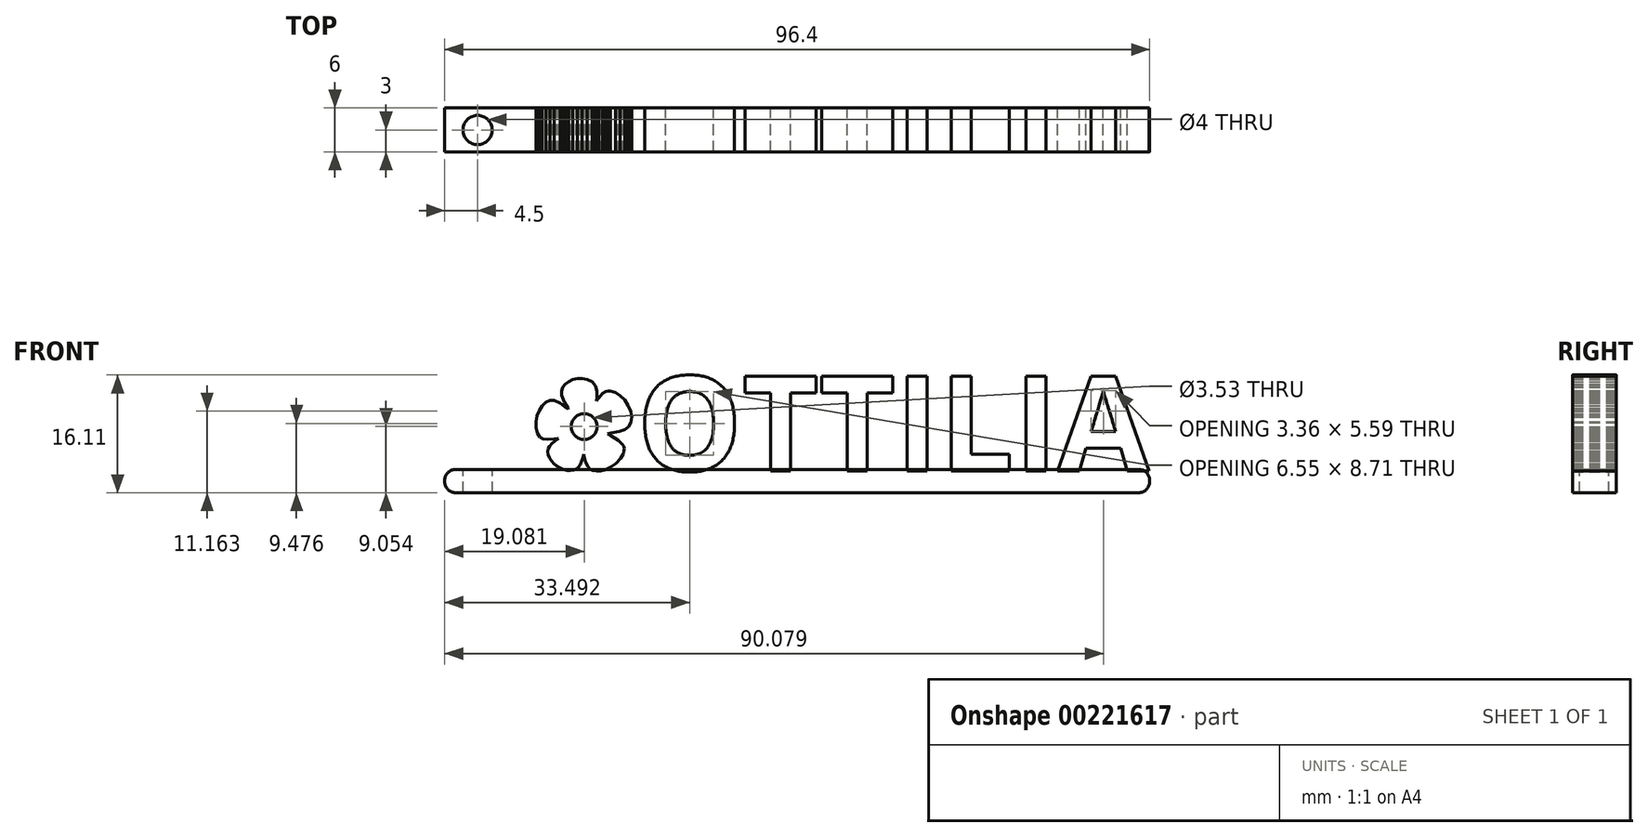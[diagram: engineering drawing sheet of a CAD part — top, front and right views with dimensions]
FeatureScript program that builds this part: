
annotation { "Feature Type Name" : "Feature", "Feature Type Description" : "" }
export const myFeature = defineFeature(function(context is Context, id is Id, definition is map)
    precondition{}
    {
        {
            var Q0;
            Q0=qCreatedBy(makeId("Front.planeOp"),FACE);
            var sketch = newSketch(context, id + "F0", { "sketchPlane" : qUnion([Q0])});
            skText(sketch, "E0", { "text": "    OTTILIA", "fontName": "OpenSans-Bold.ttf"});
            skLineSegment(sketch, "E1.0.0", {"start": v(-9.3, 0.1) * mm, "end": v(-8.53, 0.46) * mm});
            skLineSegment(sketch, "E1.0.1", {"start": v(-8.53, 0.46) * mm, "end": v(-7.79, 1.02) * mm});
            skLineSegment(sketch, "E1.0.2", {"start": v(-7.79, 1.02) * mm, "end": v(-7.18, 1.67) * mm});
            skLineSegment(sketch, "E1.0.3", {"start": v(-7.18, 1.67) * mm, "end": v(-6.78, 2.35) * mm});
            skLineSegment(sketch, "E1.0.4", {"start": v(-6.78, 2.35) * mm, "end": v(-6.68, 2.7) * mm});
            skLineSegment(sketch, "E1.0.5", {"start": v(-6.68, 2.7) * mm, "end": v(-6.67, 3.02) * mm});
            skLineSegment(sketch, "E1.0.6", {"start": v(-6.67, 3.02) * mm, "end": v(-6.73, 3.33) * mm});
            skLineSegment(sketch, "E1.0.7", {"start": v(-6.73, 3.33) * mm, "end": v(-6.89, 3.62) * mm});
            skLineSegment(sketch, "E1.0.8", {"start": v(-6.89, 3.62) * mm, "end": v(-7.48, 4.2) * mm});
            skLineSegment(sketch, "E1.0.9", {"start": v(-7.48, 4.2) * mm, "end": v(-8.5, 4.79) * mm});
            skLineSegment(sketch, "E1.0.10", {"start": v(-8.5, 4.79) * mm, "end": v(-8.93, 5.06) * mm});
            skLineSegment(sketch, "E1.0.11", {"start": v(-8.93, 5.06) * mm, "end": v(-8.42, 5.16) * mm});
            skLineSegment(sketch, "E1.0.12", {"start": v(-8.42, 5.16) * mm, "end": v(-7.31, 5.37) * mm});
            skLineSegment(sketch, "E1.0.13", {"start": v(-7.31, 5.37) * mm, "end": v(-6.55, 5.65) * mm});
            skLineSegment(sketch, "E1.0.14", {"start": v(-6.55, 5.65) * mm, "end": v(-6.05, 6.04) * mm});
            skLineSegment(sketch, "E1.0.15", {"start": v(-6.05, 6.04) * mm, "end": v(-5.76, 6.58) * mm});
            skLineSegment(sketch, "E1.0.16", {"start": v(-5.76, 6.58) * mm, "end": v(-5.64, 7.33) * mm});
            skLineSegment(sketch, "E1.0.17", {"start": v(-5.64, 7.33) * mm, "end": v(-5.78, 8.14) * mm});
            skLineSegment(sketch, "E1.0.18", {"start": v(-5.78, 8.14) * mm, "end": v(-6.1, 8.93) * mm});
            skLineSegment(sketch, "E1.0.19", {"start": v(-6.1, 8.93) * mm, "end": v(-6.6, 9.67) * mm});
            skLineSegment(sketch, "E1.0.20", {"start": v(-6.6, 9.67) * mm, "end": v(-7.2, 10.28) * mm});
            skLineSegment(sketch, "E1.0.21", {"start": v(-7.2, 10.28) * mm, "end": v(-7.86, 10.72) * mm});
            skLineSegment(sketch, "E1.0.22", {"start": v(-7.86, 10.72) * mm, "end": v(-8.55, 10.93) * mm});
            skLineSegment(sketch, "E1.0.23", {"start": v(-8.55, 10.93) * mm, "end": v(-8.88, 10.93) * mm});
            skLineSegment(sketch, "E1.0.24", {"start": v(-8.88, 10.93) * mm, "end": v(-9.2, 10.85) * mm});
            skLineSegment(sketch, "E1.0.25", {"start": v(-9.2, 10.85) * mm, "end": v(-9.65, 10.56) * mm});
            skLineSegment(sketch, "E1.0.26", {"start": v(-9.65, 10.56) * mm, "end": v(-10.14, 9.98) * mm});
            skLineSegment(sketch, "E1.0.27", {"start": v(-10.14, 9.98) * mm, "end": v(-10.45, 9.58) * mm});
            skLineSegment(sketch, "E1.0.28", {"start": v(-10.45, 9.58) * mm, "end": v(-10.4, 10.03) * mm});
            skLineSegment(sketch, "E1.0.29", {"start": v(-10.4, 10.03) * mm, "end": v(-10.4, 10.93) * mm});
            skLineSegment(sketch, "E1.0.30", {"start": v(-10.4, 10.93) * mm, "end": v(-10.6, 11.63) * mm});
            skLineSegment(sketch, "E1.0.31", {"start": v(-10.6, 11.63) * mm, "end": v(-11.04, 12.15) * mm});
            skLineSegment(sketch, "E1.0.32", {"start": v(-11.04, 12.15) * mm, "end": v(-11.71, 12.5) * mm});
            skLineSegment(sketch, "E1.0.33", {"start": v(-11.71, 12.5) * mm, "end": v(-12.4, 12.64) * mm});
            skLineSegment(sketch, "E1.0.34", {"start": v(-12.4, 12.64) * mm, "end": v(-13.07, 12.62) * mm});
            skLineSegment(sketch, "E1.0.35", {"start": v(-13.07, 12.62) * mm, "end": v(-13.7, 12.47) * mm});
            skLineSegment(sketch, "E1.0.36", {"start": v(-13.7, 12.47) * mm, "end": v(-14.26, 12.2) * mm});
            skLineSegment(sketch, "E1.0.37", {"start": v(-14.26, 12.2) * mm, "end": v(-14.72, 11.83) * mm});
            skLineSegment(sketch, "E1.0.38", {"start": v(-14.72, 11.83) * mm, "end": v(-15.05, 11.38) * mm});
            skLineSegment(sketch, "E1.0.39", {"start": v(-15.05, 11.38) * mm, "end": v(-15.22, 10.87) * mm});
            skLineSegment(sketch, "E1.0.40", {"start": v(-15.22, 10.87) * mm, "end": v(-15.2, 10.3) * mm});
            skLineSegment(sketch, "E1.0.41", {"start": v(-15.2, 10.3) * mm, "end": v(-14.83, 9.4) * mm});
            skLineSegment(sketch, "E1.0.42", {"start": v(-14.83, 9.4) * mm, "end": v(-14.35, 8.55) * mm});
            skLineSegment(sketch, "E1.0.43", {"start": v(-14.35, 8.55) * mm, "end": v(-14.3, 8.4) * mm});
            skLineSegment(sketch, "E1.0.44", {"start": v(-14.3, 8.4) * mm, "end": v(-14.48, 8.53) * mm});
            skLineSegment(sketch, "E1.0.45", {"start": v(-14.48, 8.53) * mm, "end": v(-15.4, 9.23) * mm});
            skLineSegment(sketch, "E1.0.46", {"start": v(-15.4, 9.23) * mm, "end": v(-16.22, 9.63) * mm});
            skLineSegment(sketch, "E1.0.47", {"start": v(-16.22, 9.63) * mm, "end": v(-16.8, 9.63) * mm});
            skLineSegment(sketch, "E1.0.48", {"start": v(-16.8, 9.63) * mm, "end": v(-17.36, 9.37) * mm});
            skLineSegment(sketch, "E1.0.49", {"start": v(-17.36, 9.37) * mm, "end": v(-17.85, 8.9) * mm});
            skLineSegment(sketch, "E1.0.50", {"start": v(-17.85, 8.9) * mm, "end": v(-18.26, 8.26) * mm});
            skLineSegment(sketch, "E1.0.51", {"start": v(-18.26, 8.26) * mm, "end": v(-18.56, 7.51) * mm});
            skLineSegment(sketch, "E1.0.52", {"start": v(-18.56, 7.51) * mm, "end": v(-18.72, 6.71) * mm});
            skLineSegment(sketch, "E1.0.53", {"start": v(-18.72, 6.71) * mm, "end": v(-18.72, 5.9) * mm});
            skLineSegment(sketch, "E1.0.54", {"start": v(-18.72, 5.9) * mm, "end": v(-18.52, 5.16) * mm});
            skLineSegment(sketch, "E1.0.55", {"start": v(-18.52, 5.16) * mm, "end": v(-18.2, 4.64) * mm});
            skLineSegment(sketch, "E1.0.56", {"start": v(-18.2, 4.64) * mm, "end": v(-17.75, 4.36) * mm});
            skLineSegment(sketch, "E1.0.57", {"start": v(-17.75, 4.36) * mm, "end": v(-17.1, 4.27) * mm});
            skLineSegment(sketch, "E1.0.58", {"start": v(-17.1, 4.27) * mm, "end": v(-16.21, 4.37) * mm});
            skLineSegment(sketch, "E1.0.59", {"start": v(-16.21, 4.37) * mm, "end": v(-15.7, 4.43) * mm});
            skLineSegment(sketch, "E1.0.60", {"start": v(-15.7, 4.43) * mm, "end": v(-15.67, 4.4) * mm});
            skLineSegment(sketch, "E1.0.61", {"start": v(-15.67, 4.4) * mm, "end": v(-15.78, 4.33) * mm});
            skLineSegment(sketch, "E1.0.62", {"start": v(-15.78, 4.33) * mm, "end": v(-16.17, 4.07) * mm});
            skLineSegment(sketch, "E1.0.63", {"start": v(-16.17, 4.07) * mm, "end": v(-16.55, 3.71) * mm});
            skLineSegment(sketch, "E1.0.64", {"start": v(-16.55, 3.71) * mm, "end": v(-16.87, 3.33) * mm});
            skLineSegment(sketch, "E1.0.65", {"start": v(-16.87, 3.33) * mm, "end": v(-17.04, 3) * mm});
            skLineSegment(sketch, "E1.0.66", {"start": v(-17.04, 3) * mm, "end": v(-17.08, 2.6) * mm});
            skLineSegment(sketch, "E1.0.67", {"start": v(-17.08, 2.6) * mm, "end": v(-17.02, 2.2) * mm});
            skLineSegment(sketch, "E1.0.68", {"start": v(-17.02, 2.2) * mm, "end": v(-16.87, 1.78) * mm});
            skLineSegment(sketch, "E1.0.69", {"start": v(-16.87, 1.78) * mm, "end": v(-16.62, 1.39) * mm});
            skLineSegment(sketch, "E1.0.70", {"start": v(-16.62, 1.39) * mm, "end": v(-16.3, 1.02) * mm});
            skLineSegment(sketch, "E1.0.71", {"start": v(-16.3, 1.02) * mm, "end": v(-15.9, 0.69) * mm});
            skLineSegment(sketch, "E1.0.72", {"start": v(-15.9, 0.69) * mm, "end": v(-15.45, 0.4) * mm});
            skLineSegment(sketch, "E1.0.73", {"start": v(-15.45, 0.4) * mm, "end": v(-14.95, 0.2) * mm});
            skLineSegment(sketch, "E1.0.74", {"start": v(-14.95, 0.2) * mm, "end": v(-14.44, 0.06) * mm});
            skLineSegment(sketch, "E1.0.75", {"start": v(-14.44, 0.06) * mm, "end": v(-13.98, 0.02) * mm});
            skLineSegment(sketch, "E1.0.76", {"start": v(-13.98, 0.02) * mm, "end": v(-13.58, 0.08) * mm});
            skLineSegment(sketch, "E1.0.77", {"start": v(-13.58, 0.08) * mm, "end": v(-13.23, 0.23) * mm});
            skLineSegment(sketch, "E1.0.78", {"start": v(-13.23, 0.23) * mm, "end": v(-12.92, 0.49) * mm});
            skLineSegment(sketch, "E1.0.79", {"start": v(-12.92, 0.49) * mm, "end": v(-12.67, 0.84) * mm});
            skLineSegment(sketch, "E1.0.80", {"start": v(-12.67, 0.84) * mm, "end": v(-12.46, 1.28) * mm});
            skLineSegment(sketch, "E1.0.81", {"start": v(-12.46, 1.28) * mm, "end": v(-12.3, 1.83) * mm});
            skLineSegment(sketch, "E1.0.82", {"start": v(-12.3, 1.83) * mm, "end": v(-12.19, 2.26) * mm});
            skLineSegment(sketch, "E1.0.83", {"start": v(-12.19, 2.26) * mm, "end": v(-12.13, 2.1) * mm});
            skLineSegment(sketch, "E1.0.84", {"start": v(-12.13, 2.1) * mm, "end": v(-12.01, 1.53) * mm});
            skLineSegment(sketch, "E1.0.85", {"start": v(-12.01, 1.53) * mm, "end": v(-11.82, 1) * mm});
            skLineSegment(sketch, "E1.0.86", {"start": v(-11.82, 1) * mm, "end": v(-11.6, 0.55) * mm});
            skLineSegment(sketch, "E1.0.87", {"start": v(-11.6, 0.55) * mm, "end": v(-11.35, 0.26) * mm});
            skLineSegment(sketch, "E1.0.88", {"start": v(-11.35, 0.26) * mm, "end": v(-10.95, 0.05) * mm});
            skLineSegment(sketch, "E1.0.89", {"start": v(-10.95, 0.05) * mm, "end": v(-10.46, -0.04) * mm});
            skLineSegment(sketch, "E1.0.90", {"start": v(-10.46, -0.04) * mm, "end": v(-9.9, -0.03) * mm});
            skLineSegment(sketch, "E1.0.91", {"start": v(-9.9, -0.03) * mm, "end": v(-9.3, 0.1) * mm});
            skCircle(sketch, "E2", {"center": v(-12.12, 6.05) * mm, "radius": 1.77 * mm});
            skLineSegment(sketch, "E3.direction1", {"start": v(-16.3, 1.02) * mm, "end": v(42.4, 1.02) * mm, "construction": true});
            const initialGuessF0  = {"E0": [-0.0237, 0, 1, 0, 0.01302]};
            skSetInitialGuess(sketch, initialGuessF0);
            skSolve(sketch);
        }
        {
            var Q0;
            Q0=qSketchRegion(id+"F0",true);
            extrude(context, id + "F1", {"entities" : qUnion([Q0]), "endBound" : BoundingType.SYMMETRIC, "depth" : 6 * mm});
        }
        {
            var Q0;
            Q0=qCreatedBy(makeId("Top.planeOp"),FACE);
            var sketch = newSketch(context, id + "F2", { "sketchPlane" : qUnion([Q0])});
            skLineSegment(sketch, "E4.bottom", {"start": v(-23.7, 3) * mm, "end": v(65.2, 3) * mm});
            skLineSegment(sketch, "E4.top", {"start": v(-23.7, -3) * mm, "end": v(65.2, -3) * mm});
            skLineSegment(sketch, "E4.left", {"start": v(-23.7, 3) * mm, "end": v(-23.7, -3) * mm});
            skLineSegment(sketch, "E4.right", {"start": v(65.2, 3) * mm, "end": v(65.2, -3) * mm});
            skSolve(sketch);
        }
        {
            var Q0;
            Q0=makeQuery(id+"F2.imprint","IMPRINT",FACE,{"disambiguationData":[TD([[makeQuery(id+"F2.imprint","IMPRINT",EDGE,{"derivedFrom":sQuery(id+"F2.wireOp",EDGE,"E4.bottom")}),-1.0]])]});
            extrude(context, id + "F3", {"entities" : qUnion([Q0]), "depth" : 0.2 * mm});
        }
        {
            var Q0;
            Q0=makeQuery(id+"F3.opExtrude","CAP_FACE",FACE,{"disambiguationData":[OSD([sQuery(id+"F2.wireOp",EDGE,"E4.bottom"),sQuery(id+"F2.wireOp",EDGE,"E4.top"),sQuery(id+"F2.wireOp",EDGE,"E4.left"),sQuery(id+"F2.wireOp",EDGE,"E4.right")])],"isStart":true});
            extrude(context, id + "F4", {"entities" : qUnion([Q0]), "depth" : 3 * mm});
        }
        {
            var Q0;
            {var subQ0=sQuery(id+"F2.wireOp",EDGE,"E4.left");Q0=makeQuery(id+"FaVoHrOpcFZXiYX_6.opBoolean","MERGE",FACE,{"derivedFrom":[makeQuery(id+"F3.opExtrude","SWEPT_FACE",FACE,{"disambiguationData":[OSD([subQ0])]}),makeQuery(id+"F4.opExtrude","SWEPT_FACE",FACE,{"disambiguationData":[OSD([subQ0])]})]});}
            var sketch = newSketch(context, id + "F5", { "sketchPlane" : qUnion([Q0])});
            skLineSegment(sketch, "E5.bottom", {"start": v(-3, -3) * mm, "end": v(3, -3) * mm});
            skLineSegment(sketch, "E5.top", {"start": v(-3, 0.2) * mm, "end": v(3, 0.2) * mm});
            skLineSegment(sketch, "E5.left", {"start": v(-3, -3) * mm, "end": v(-3, 0.2) * mm});
            skLineSegment(sketch, "E5.right", {"start": v(3, -3) * mm, "end": v(3, 0.2) * mm});
            skSolve(sketch);
        }
        {
            var Q0;
            Q0=qSketchRegion(id+"F5",true);
            extrude(context, id + "F6", {"entities" : qUnion([Q0]), "operationType" : NewBodyOperationType.ADD, "depth" : 7.5 * mm});
        }
        {
            var Q0;
            Q0=makeQuery(id+"F6.opExtrude","CAP_EDGE",EDGE,{"disambiguationData":[OSD([sQuery(id+"F5.wireOp",EDGE,"E5.bottom")])],"isStart":false});
            var Q1;
            Q1=makeQuery(id+"F6.opExtrude","CAP_EDGE",EDGE,{"disambiguationData":[OSD([sQuery(id+"F5.wireOp",EDGE,"E5.top")])],"isStart":false});
            var Q2;
            Q2=makeQuery(id+"F4.opExtrude","CAP_EDGE",EDGE,{"disambiguationData":[OSD([sQuery(id+"F2.wireOp",EDGE,"E4.right")])],"isStart":false});
            fillet(context, id + "F7", {"entities" : qUnion([Q0, Q1, Q2]), "radius" : 1.5 * mm, "tangentPropagation" : true, "allowEdgeOverflow" : false});
        }
        {
            var Q0;
            {var subQ19=sQuery(id+"F2.wireOp",EDGE,"E4.top");var subQ20=sQuery(id+"F2.wireOp",EDGE,"E4.bottom");var subQ63=sQuery(id+"F0.wireOp",EDGE,"E0.sketch_text.stroke-2");var subQ66=sQuery(id+"F2.wireOp",EDGE,"E4.left");Q0=makeQuery(id+"F6.boolean.opBoolean","MERGE",FACE,{"derivedFrom":[makeQuery(id+"FaVoHrOpcFZXiYX_6.opBoolean","SPLIT",FACE,{"disambiguationData":[TD([makeQuery(id+"F1.opExtrude","SWEPT_FACE",FACE,{"disambiguationData":[OSD([subQ63])]})])],"derivedFrom":makeQuery(id+"F3.opExtrude","CAP_FACE",FACE,{"disambiguationData":[OSD([subQ20,subQ19,subQ66,sQuery(id+"F2.wireOp",EDGE,"E4.right")])],"isStart":false})}),makeQuery(id+"F6.opExtrude","SWEPT_FACE",FACE,{"disambiguationData":[OSD([sQuery(id+"F5.wireOp",EDGE,"E5.top")])]})]});}
            var sketch = newSketch(context, id + "F8", { "sketchPlane" : qUnion([Q0])});
            skCircle(sketch, "E6", {"center": v(-26.7, 0) * mm, "radius": 2 * mm});
            skSolve(sketch);
        }
        {
            var Q0;
            Q0=makeQuery(id+"F8.imprint","IMPRINT",FACE,{"disambiguationData":[TD([[makeQuery(id+"F8.imprint","IMPRINT",EDGE,{"derivedFrom":sQuery(id+"F8.wireOp",EDGE,"E6")}),1.0]])]});
            extrude(context, id + "F9", {"entities" : qUnion([Q0]), "operationType" : NewBodyOperationType.REMOVE, "oppositeDirection" : true, "depth" : 4 * mm});
        }
        {
            var Q0;
            Q0=makeQuery(id+"F3.opExtrude","CAP_EDGE",EDGE,{"disambiguationData":[OSD([sQuery(id+"F2.wireOp",EDGE,"E4.right")])],"isStart":false});
            fillet(context, id + "F10", {"entities" : qUnion([Q0]), "radius" : 1.5 * mm, "tangentPropagation" : true, "allowEdgeOverflow" : false});
        }
    });
